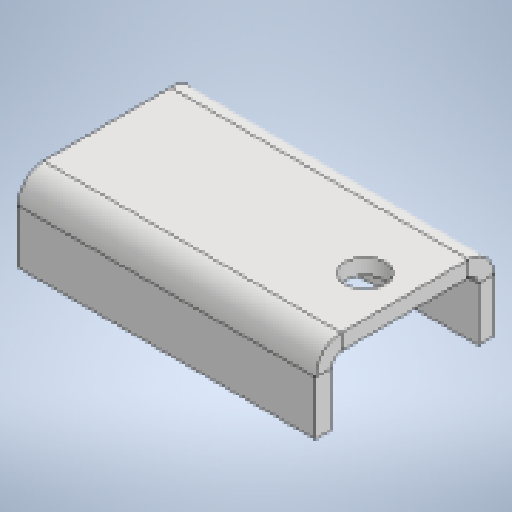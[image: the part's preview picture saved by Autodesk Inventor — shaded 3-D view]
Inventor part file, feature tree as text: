
AUTODESK INVENTOR PART (.ipt)
format: ipt  version: 2025.1 (Build 291241020, 241B)  size: 192,512 bytes
history: native  units: mm
features: sheet_metal_op x4, other x3, sketch x2
ambient origin geometry x8: Origin, YZ Plane, XZ Plane, XY Plane, X Axis, Y Axis, Z Axis, Center Point
bodies: Solid1 (feature_tree)
feature tree (9):
  sheet_metal_op  "Face1"
  sheet_metal_op  "Flange2"
  sketch  "Sketch1"  dims[d0=150.0mm]
  other  "Plate1"
  sketch  "Sketch6"  dims[d1=90.0mm d2=8.0mm d23=20.0mm d25=20.0mm d26=20.0mm d30=8.0mm d31=4.0mm d32=16.0mm d33=5.0mm d34=40.0mm d35=90.0deg d36=5.0mm d37=32.0mm d38=8.0mm d39=5.0mm]
  other  "Plate3"
  sheet_metal_op  "Bend2"
  sheet_metal_op  "Corner2"
  other  "Definition1"
